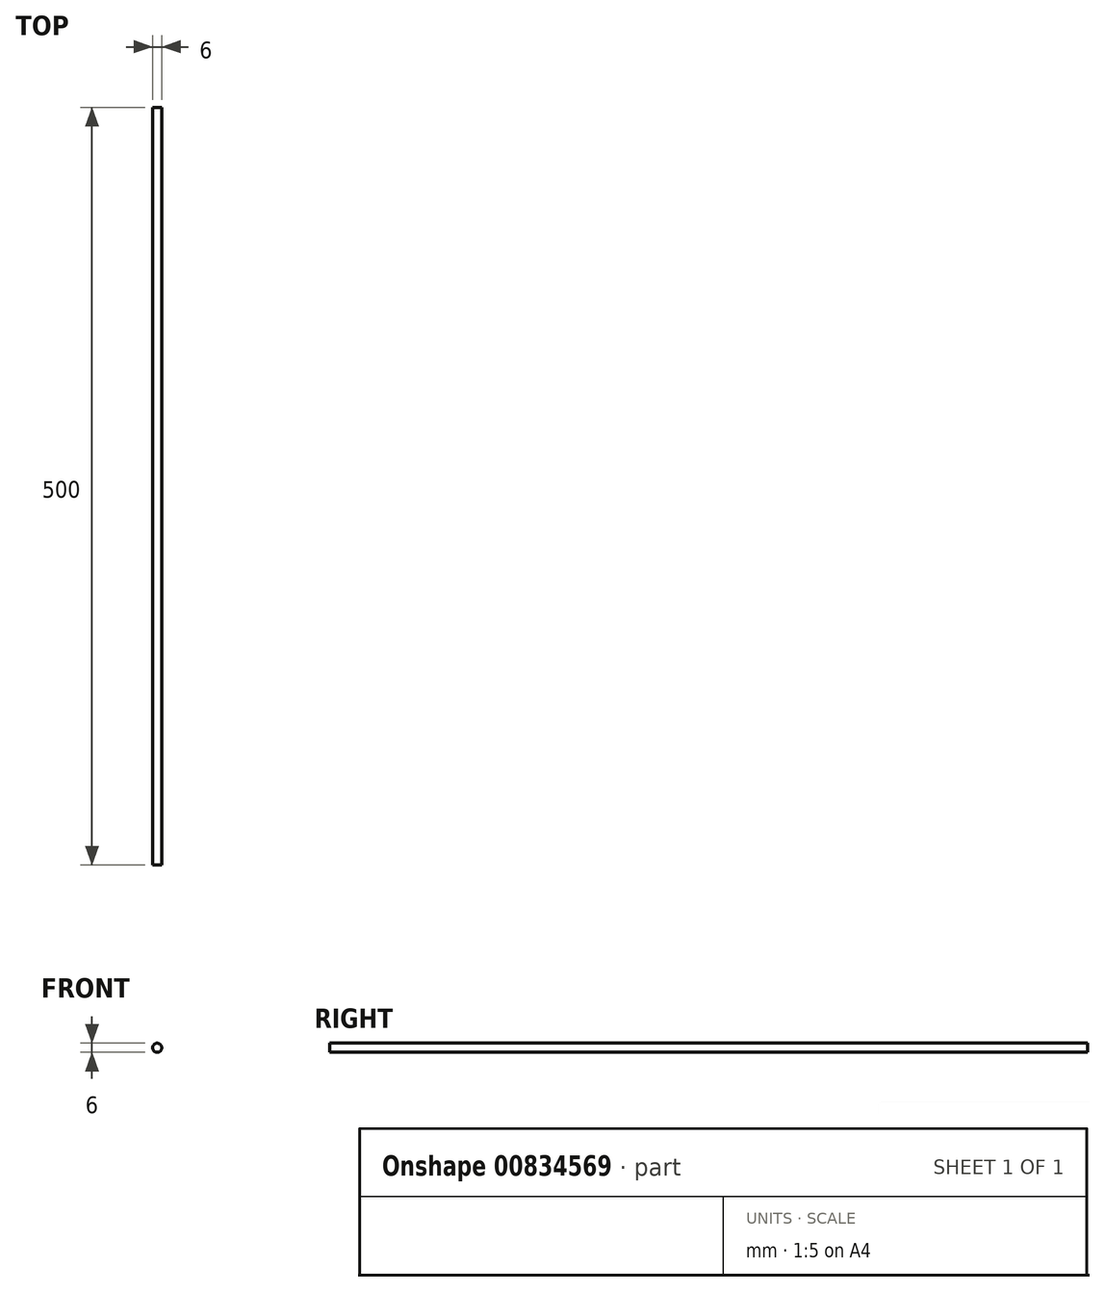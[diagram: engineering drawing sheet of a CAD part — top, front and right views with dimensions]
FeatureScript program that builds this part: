
annotation { "Feature Type Name" : "Feature", "Feature Type Description" : "" }
export const myFeature = defineFeature(function(context is Context, id is Id, definition is map)
    precondition{}
    {
        {
            var Q0;
            Q0=qCreatedBy(makeId("Front.planeOp"),FACE);
            var sketch = newSketch(context, id + "F0", { "sketchPlane" : qUnion([Q0])});
            skCircle(sketch, "E0", {"center": v(0, 0) * mm, "radius": 3 * mm});
            skSolve(sketch);
        }
        {
            var Q0;
            Q0=makeQuery(id+"F0.imprint","IMPRINT",FACE,{"disambiguationData":[TD([[makeQuery(id+"F0.imprint","IMPRINT",EDGE,{"derivedFrom":sQuery(id+"F0.wireOp",EDGE,"E0")}),1.0]])]});
            extrude(context, id + "F1", {"entities" : qUnion([Q0]), "depth" : 500 * mm, "offsetDistance" : 25 * mm});
        }
    });
